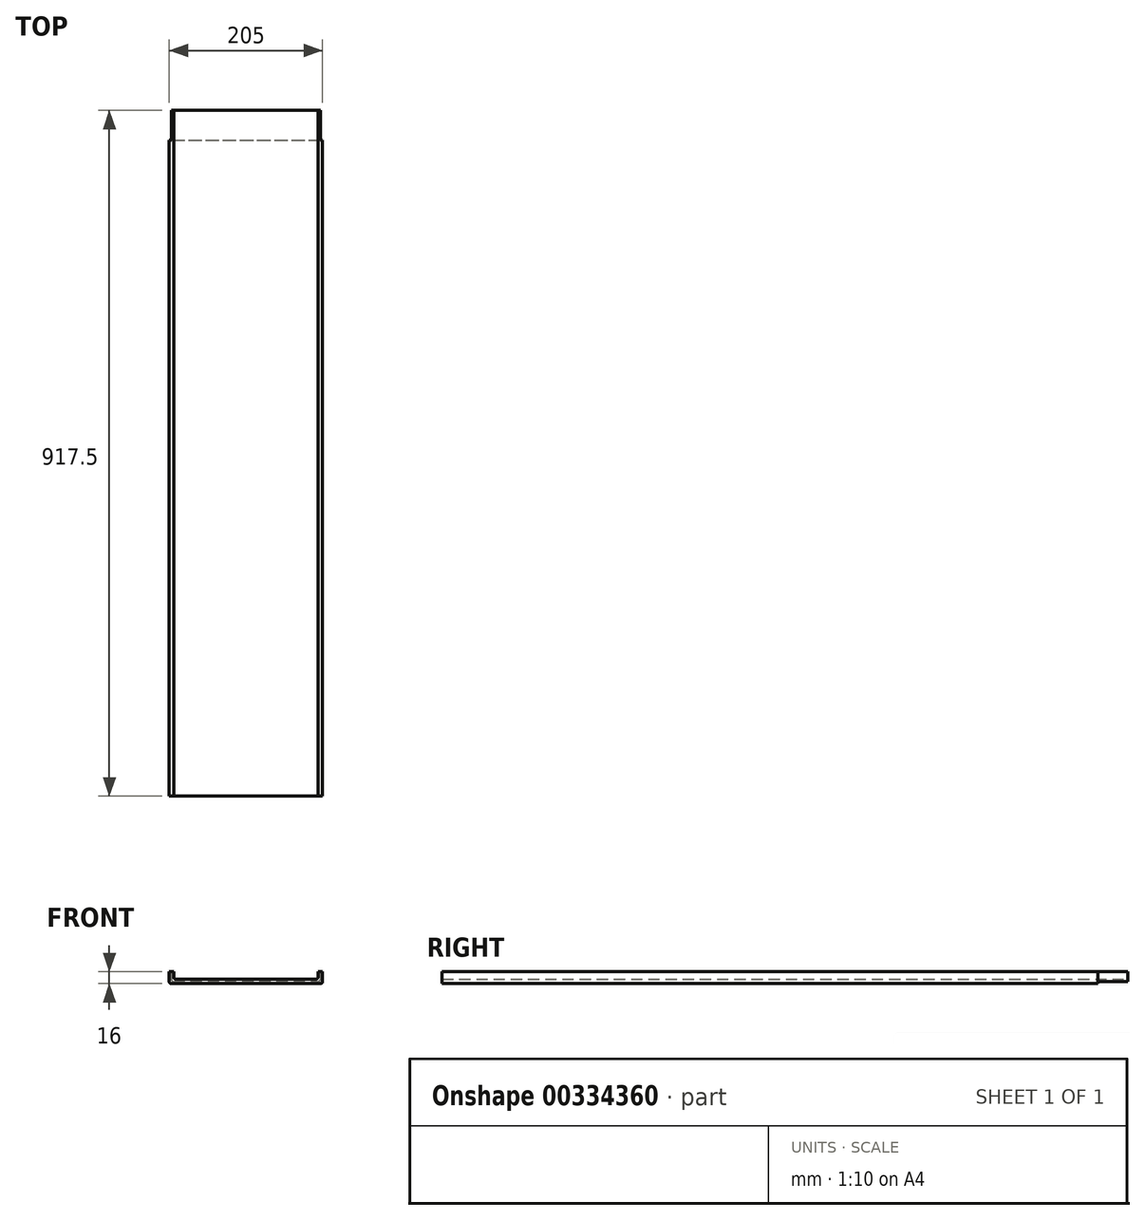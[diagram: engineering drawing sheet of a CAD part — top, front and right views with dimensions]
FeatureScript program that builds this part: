
annotation { "Feature Type Name" : "Feature", "Feature Type Description" : "" }
export const myFeature = defineFeature(function(context is Context, id is Id, definition is map)
    precondition{}
    {
        {
            var Q0;
            Q0=qCreatedBy(makeId("Front.planeOp"),FACE);
            var sketch = newSketch(context, id + "F0", { "sketchPlane" : qUnion([Q0])});
            skLineSegment(sketch, "E0.top", {"start": v(-100, -16) * mm, "end": v(100, -16) * mm});
            skLineSegment(sketch, "E0.left", {"start": v(-102.5, 16) * mm, "end": v(-102.5, -13.5) * mm});
            skLineSegment(sketch, "E0.right", {"start": v(102.5, 0) * mm, "end": v(102.5, -13.5) * mm});
            skPoint(sketch, "E0.middle", {"position": v(0, 0) * mm});
            skLineSegment(sketch, "E1.top", {"start": v(-97, -13) * mm, "end": v(97, -13) * mm});
            skLineSegment(sketch, "E1.left", {"start": v(-99.5, 13) * mm, "end": v(-99.5, -10.5) * mm});
            skLineSegment(sketch, "E1.right", {"start": v(99.5, 0) * mm, "end": v(99.5, -10.5) * mm});
            skLineSegment(sketch, "E2.top", {"start": v(-94, -10) * mm, "end": v(94, -10) * mm});
            skLineSegment(sketch, "E2.left", {"start": v(-96.5, 10) * mm, "end": v(-96.5, -7.5) * mm});
            skLineSegment(sketch, "E2.right", {"start": v(96.5, 0) * mm, "end": v(96.5, -7.5) * mm});
            skLineSegment(sketch, "E3", {"start": v(102.5, 0) * mm, "end": v(96.5, 0) * mm});
            skPoint(sketch, "E4.visualSharp", {"position": v(96.5, -10) * mm});
            skArc(sketch, "E4.filletArc", {"start": v(94, -10) * mm, "mid": v(95.77, -9.27) * mm, "end": v(96.5, -7.5) * mm});
            skPoint(sketch, "E5.visualSharp", {"position": v(99.5, -13) * mm});
            skArc(sketch, "E5.filletArc", {"start": v(97, -13) * mm, "mid": v(98.77, -12.27) * mm, "end": v(99.5, -10.5) * mm});
            skPoint(sketch, "E6.visualSharp", {"position": v(102.5, -16) * mm});
            skArc(sketch, "E6.filletArc", {"start": v(100, -16) * mm, "mid": v(101.77, -15.27) * mm, "end": v(102.5, -13.5) * mm});
            skArc(sketch, "E7.MirrorCS", {"start": v(-100, -16) * mm, "mid": v(-101.77, -15.27) * mm, "end": v(-102.5, -13.5) * mm});
            skPoint(sketch, "E8.MirrorP", {"position": v(-96.5, -10) * mm});
            skLineSegment(sketch, "E9.MirrorCS", {"start": v(96.5, -10) * mm, "end": v(-94, -10) * mm});
            skPoint(sketch, "E10.MirrorP", {"position": v(-99.5, -13) * mm});
            skArc(sketch, "E11.MirrorCS", {"start": v(-97, -13) * mm, "mid": v(-98.77, -12.27) * mm, "end": v(-99.5, -10.5) * mm});
            skArc(sketch, "E12.MirrorCS", {"start": v(-94, -10) * mm, "mid": v(-95.77, -9.27) * mm, "end": v(-96.5, -7.5) * mm});
            skPoint(sketch, "E13.MirrorP", {"position": v(-102.5, -16) * mm});
            skLineSegment(sketch, "E14.MirrorCS", {"start": v(-96.5, 0) * mm, "end": v(-96.5, -7.5) * mm});
            skLineSegment(sketch, "E15.MirrorCS", {"start": v(102.5, -16) * mm, "end": v(-100, -16) * mm});
            skLineSegment(sketch, "E16.MirrorCS", {"start": v(-102.5, 0) * mm, "end": v(-102.5, -13.5) * mm});
            skLineSegment(sketch, "E17.MirrorCS", {"start": v(99.5, -13) * mm, "end": v(-97, -13) * mm});
            skLineSegment(sketch, "E18.MirrorCS", {"start": v(-99.5, 0) * mm, "end": v(-99.5, -10.5) * mm});
            skPoint(sketch, "E0.bottom.end.orphan", {"position": v(102.5, 16) * mm});
            skPoint(sketch, "E1.bottom.end.orphan", {"position": v(99.5, 13) * mm});
            skPoint(sketch, "E2.bottom.end.orphan", {"position": v(96.5, 10) * mm});
            skLineSegment(sketch, "E19.trimOffspring", {"start": v(-96.5, 0) * mm, "end": v(-102.5, 0) * mm});
            skPoint(sketch, "E20.orphan", {"position": v(-102.5, 16) * mm});
            skPoint(sketch, "E21.orphan", {"position": v(-99.5, 13) * mm});
            skPoint(sketch, "E22.orphan", {"position": v(-96.5, 10) * mm});
            skSolve(sketch);
        }
        {
            var Q0;
            Q0=qSketchRegion(id+"F0",true);
            extrude(context, id + "F1", {"entities" : qUnion([Q0]), "depth" : 917.5 * mm});
        }
        {
            var Q0;
            {var subQ6=sQuery(id+"F0.wireOp",EDGE,"E0.right");Q0=makeQuery(id+"F0.imprint","IMPRINT",FACE,{"disambiguationData":[TD([[makeQuery(id+"F0.imprint","IMPRINT",EDGE,{"derivedFrom":subQ6}),-1.0]])]});}
            extrude(context, id + "F2", {"entities" : qUnion([Q0]), "operationType" : NewBodyOperationType.REMOVE, "depth" : 40 * mm});
        }
    });
